# Revit family: Furniture-Mirror-KOHLER-Essential-K-31371_1
name_source: partatom
category: Specialty Equipment
units: mm (PartAtom-declared; Revit-internal decimal feet)

## family parameters
Cut with Voids When Loaded = No
Host = Face
Maintain Annotation Orientation = No
OmniClass Number = 23.21.37.13.15
OmniClass Title = Mirrors
Part Type = Normal
Room Calculation Point = No
Round Connector Dimension = Use Diameter
Shared = No

## types (4) — shared parameters
ADA Compliant = No
Assembly Code = E20
Date Modified = 07/04/2022
Default Elevation = 60"
Description = Capsule 18 inch x 36 inch
Height = 36"
Length = 18"
Manufacturer = Kohler Co.
Master Format 2014 = 06 41 93
Master Format 2014 Name = Cabinet and Drawer Hardware
Material = Premium Metal Construction
Product Documentation Link = https://www.us.kohler.com
Product Name = Essential
Product Page URL = http://www.us.kohler.com
URL = http://www.us.kohler.com
WaterSense Certified = No
Width = 1 3/8"

## per-type parameters (varying)
| type | Finish | Model | Type |
| CPL-Polished Chrome | KOHLER-Metal-CPL-Polished_Chrome | K-31371-CPL | 1 |
| BNL-Brushed Nickel | KOHLER-Metal-BNL-Brushed_Nickel | K-31371-BNL | 2 |
| BGL-Moderne Brushed Gold | KOHLER-Metal-BGL-Moderne_Brushed_Gold | K-31371-BGL | 3 |
| BLL-Matte Black | KOHLER-Metal-BLL-Matte_Black | K-31371-BLL | 4 |

## geometry (parser evidence)
native form markers: Sweep x6
no freeform markers — native parametric forms only
